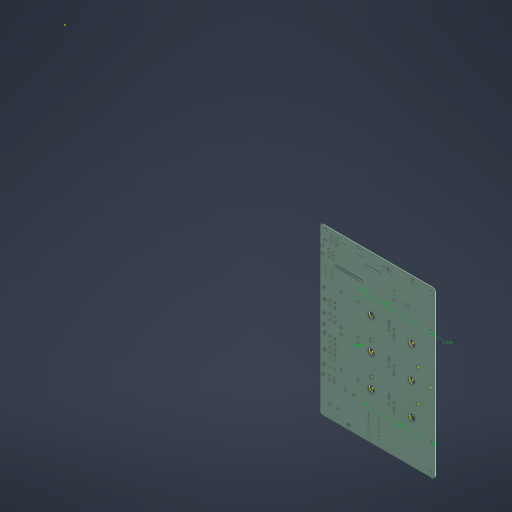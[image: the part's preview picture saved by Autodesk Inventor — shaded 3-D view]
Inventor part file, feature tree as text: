
AUTODESK INVENTOR PART (.ipt)
format: ipt  version: 2024.2 (Build 282272000, 272)  size: 470,016 bytes
history: native  units: in
note: dims shown in document units (in); Inventor stores cm internally (conversion verified against a paired STEP export)
features: other x3, sketch x1
ambient origin geometry x8: Origin, YZ Plane, XZ Plane, XY Plane, X Axis, Y Axis, Z Axis, Center Point
bodies: Solid1 (feature_tree)
feature tree (4):
  other  "HV servo drive v1_PCB.ipt"
  sketch  "Sketch1"  dims[d0=0.3937in d1=3.42in d2=4.0in d3=3.47in d4=0.02in]
  other  "Solid1::HV servo drive v1_PCB.ipt"
  other  "TaggingFeature1"
